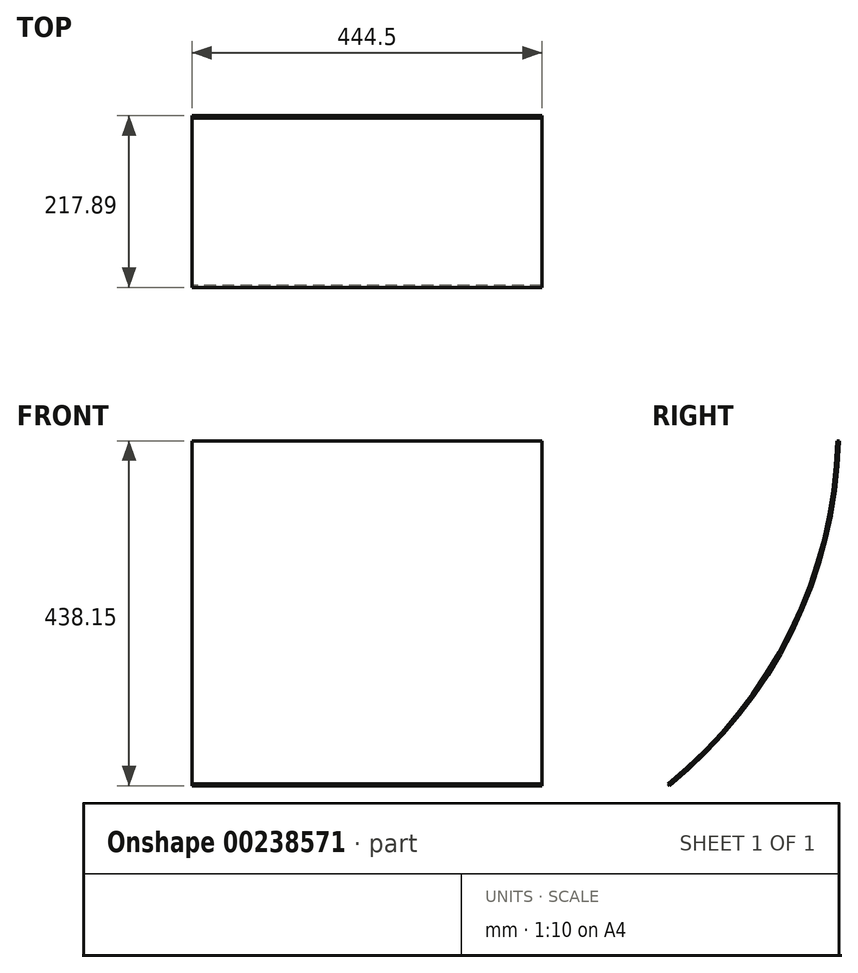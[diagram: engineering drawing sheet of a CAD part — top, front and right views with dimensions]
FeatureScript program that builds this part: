
annotation { "Feature Type Name" : "Feature", "Feature Type Description" : "" }
export const myFeature = defineFeature(function(context is Context, id is Id, definition is map)
    precondition{}
    {
        {
            var Q0;
            Q0=qCreatedBy(makeId("Right.planeOp"),FACE);
            var sketch = newSketch(context, id + "F0", { "sketchPlane" : qUnion([Q0])});
            skLineSegment(sketch, "E0.bottom", {"start": v(36.34, 226.9) * mm, "end": v(39.51, 226.9) * mm});
            skArc(sketch, "E1", {"start": v(-176.39, -211.26) * mm, "mid": v(-20.3, -15.9) * mm, "end": v(39.51, 226.9) * mm});
            skArc(sketch, "E2.0", {"start": v(-178.38, -208.8) * mm, "mid": v(-23.14, -14.5) * mm, "end": v(36.34, 226.97) * mm});
            skLineSegment(sketch, "E3", {"start": v(-176.39, -211.26) * mm, "end": v(-178.38, -208.8) * mm});
            skSolve(sketch);
        }
        {
            var Q0;
            Q0 = qSketchRegion(id + "F0", true);
            extrude(context, id + "F1", {"entities" : qUnion([Q0]), "depth" : 444.5 * mm});
        }
    });
